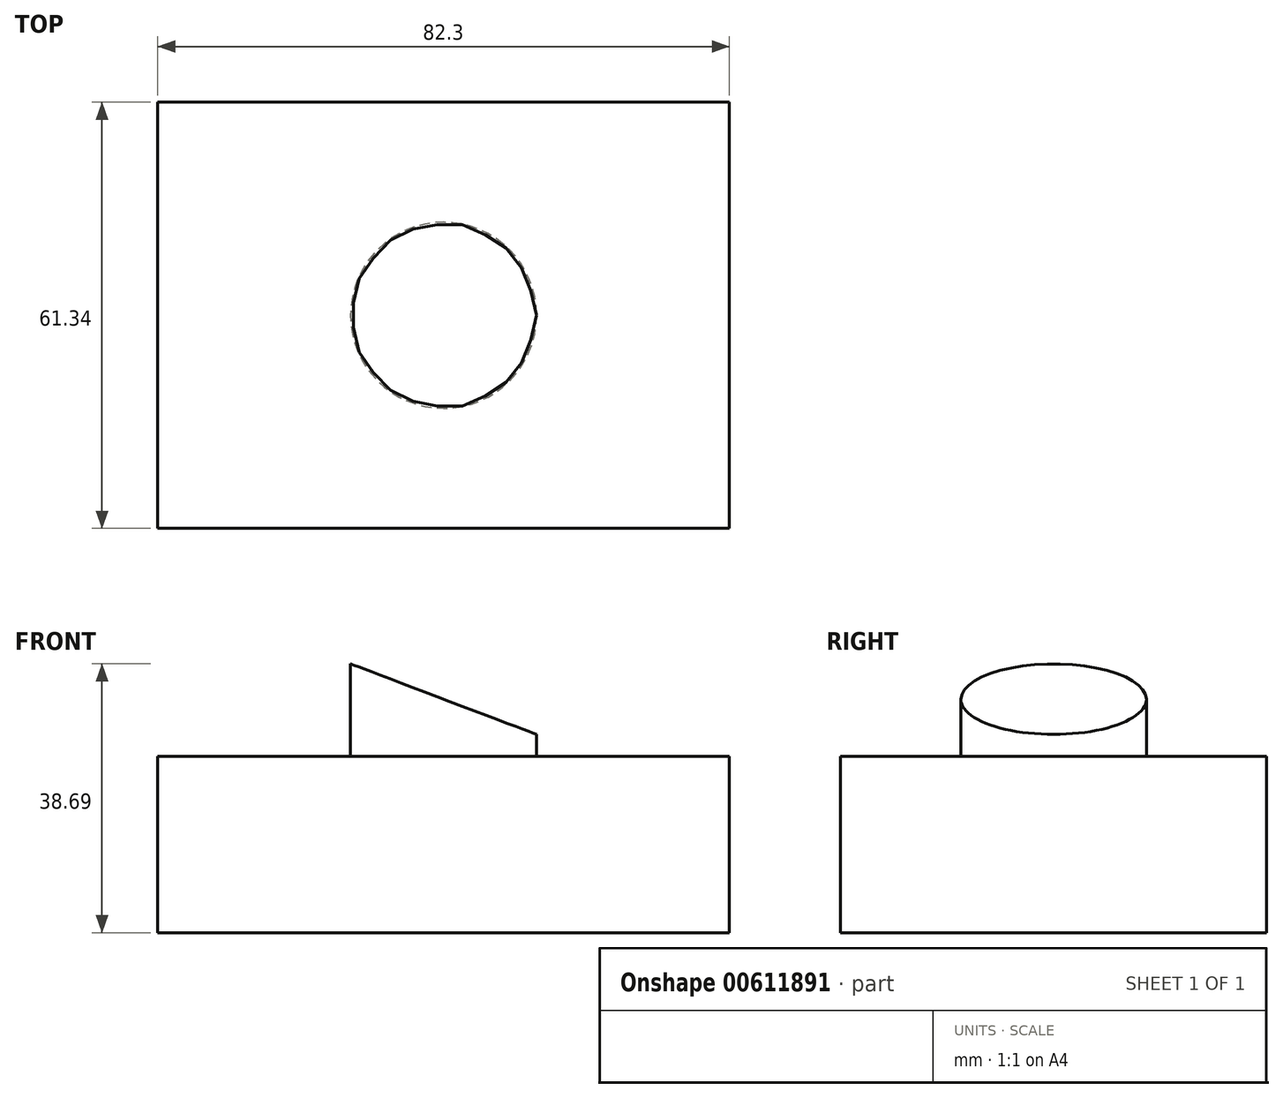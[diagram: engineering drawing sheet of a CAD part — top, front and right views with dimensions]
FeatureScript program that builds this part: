
annotation { "Feature Type Name" : "Feature", "Feature Type Description" : "" }
export const myFeature = defineFeature(function(context is Context, id is Id, definition is map)
    precondition{}
    {
        {
            var Q0;
            Q0=qCreatedBy(makeId("Top.planeOp"),FACE);
            var sketch = newSketch(context, id + "F0", { "sketchPlane" : qUnion([Q0])});
            skLineSegment(sketch, "E0.bottom", {"start": v(41.15, -30.67) * mm, "end": v(-41.15, -30.67) * mm});
            skLineSegment(sketch, "E0.top", {"start": v(41.15, 30.67) * mm, "end": v(-41.15, 30.67) * mm});
            skLineSegment(sketch, "E0.left", {"start": v(41.15, -30.67) * mm, "end": v(41.15, 30.67) * mm});
            skLineSegment(sketch, "E0.right", {"start": v(-41.15, -30.67) * mm, "end": v(-41.15, 30.67) * mm});
            skPoint(sketch, "E0.middle", {"position": v(0, 0) * mm});
            skSolve(sketch);
        }
        {
            var Q0;
            Q0 = qSketchRegion(id + "F0", true);
            extrude(context, id + "F1", {"entities" : qUnion([Q0]), "depth" : 25.4 * mm, "offsetDistance" : 25.4 * mm});
        }
        {
            var Q0;
            Q0=makeQuery(id+"F1.opExtrude","CAP_FACE",FACE,{"disambiguationData":[OSD([sQuery(id+"F0.wireOp",EDGE,"E0.bottom"),sQuery(id+"F0.wireOp",EDGE,"E0.top"),sQuery(id+"F0.wireOp",EDGE,"E0.left"),sQuery(id+"F0.wireOp",EDGE,"E0.right")])],"isStart":false});
            var sketch = newSketch(context, id + "F2", { "sketchPlane" : qUnion([Q0])});
            skCircle(sketch, "E1", {"center": v(0, 0) * mm, "radius": 13.38 * mm});
            skSolve(sketch);
        }
        {
            var Q0;
            Q0 = qSketchRegion(id + "F2", true);
            extrude(context, id + "F3", {"entities" : qUnion([Q0]), "operationType" : NewBodyOperationType.ADD, "depth" : 15 * mm, "offsetDistance" : 25.4 * mm});
        }
        {
            var Q0;
            Q0=qCreatedBy(makeId("Front.planeOp"),FACE);
            var sketch = newSketch(context, id + "F4", { "sketchPlane" : qUnion([Q0])});
            skLineSegment(sketch, "E2", {"start": v(-21.93, 41.93) * mm, "end": v(18.07, 26.76) * mm});
            skLineSegment(sketch, "E3", {"start": v(18.07, 26.76) * mm, "end": v(18.07, 41.93) * mm});
            skLineSegment(sketch, "E4", {"start": v(18.07, 41.93) * mm, "end": v(-21.93, 41.93) * mm});
            skSolve(sketch);
        }
        {
            var Q0;
            Q0 = qSketchRegion(id + "F4", true);
            extrude(context, id + "F5", {"entities" : qUnion([Q0]), "operationType" : NewBodyOperationType.REMOVE, "endBound" : BoundingType.SYMMETRIC, "oppositeDirection" : true, "depth" : 50.8 * mm, "offsetDistance" : 25.4 * mm});
        }
    });
